# Revit family: NAU_Naughtone_Stng_HueWIP6
name_source: partatom
category: Furniture
revit_build: Autodesk Revit 2016 (Build: 20150714_1515(x64)
units: mm (PartAtom-declared; Revit-internal decimal feet)

## family parameters
Always vertical = Yes
Cut with Voids When Loaded = No
OmniClass Number = 23.40.20.00
OmniClass Title = General Furniture and Specialties
Room Calculation Point = No
Shared = Yes
Work Plane-Based = No

## types (4) — shared parameters
Assembly Code = E2020200
AssetType = Movable
Category = Pr_40_50_12 : Chairs, seats and benches
DurationUnit = year
ExpectedLife = 7
Finish = Fabric upholstery, wooden table top with oak/walnut veneer, white/black MFMDF top with reverse chamfer, white/black/RAL EPC steel frame
IfcExportAs = IfcFurnishingElementType
IfcExportType = CHAIR
Keynote = Pr_40_50_12
ManufacturerName = Naughtone
ManufacturerURL = www.naughtone.com/
Material = Fabric, plywood frame, foam, steel legs, wooden table top
NBSDescription = Seating
NBSReference = 45-35-72/352
NominalLength = 1870 mm
NominalWidth = 900 mm
ProductInformation = www.naughtone.com
Shape = Rectangular
SustainabilityPerformance = FSC certifeied, SCS indoor advantage gold
URL = www.naughtone.com
Uniclass2015Code = Pr_40_50_12
Uniclass2015Title = Chairs, seats and benches
Uniclass2015Version = Products v1.14
Version = 1
WarrantyDurationLabor = 7
WarrantyDurationParts = 7
WarrantyDurationUnit = year

## per-type parameters (varying)
| type | BIMObjectName | Description | HeightOfSeatingFrame | HighestSeatingHeight | IsHighLeg | IsLeg | IsPanel | LowestSeatingHeight | Model | ModelNumber | ModelReference | Name | NominalHeight | SeatingHeight | Size |
| Hue with steel legs HUEST 1870 x 900 x 750 mm | NAU_Naughtone_Seating_Hue_WithSteelLegs | Hue with steel legs - Hue is perfect for use in narrow spaces, and is ideally suited for pre and post meeting situations. | 284 mm | 450 mm  [stored 1.47638 ft] | No | Yes | No | 450 mm  [stored 1.47638 ft] | HUEST | HUEST | Hue with steel legs - Hue is perfect for use in narrow spaces, and is ideally suited for pre and post meeting situations. | Seating_Hue_WithSteelLegs_Naughtone | 750 mm  [stored 2.46063 ft] | 450 mm  [stored 1.47638 ft] | 1870 x 900 x 750 mm |
| Hue with screen and steel legs HUESST 1870 x 900 x 1495 mm | NAU_Naughtone_Seating_Hue_WithScreenandSteelLegs | Hue with screen and steel legs - Hue is perfect for use in narrow spaces, and is ideally suited for pre and post meeting situations. | 284 mm | 450 mm  [stored 1.47638 ft] | No | Yes | Yes | 450 mm  [stored 1.47638 ft] | HUESST | HUESST | Hue with screen and steel legs - Hue is perfect for use in narrow spaces, and is ideally suited for pre and post meeting situations. | Seating_Hue_WithScreenandSteelLegs_Naughtone | 1495 mm | 450 mm  [stored 1.47638 ft] | 1870 x 900 x 1495 mm |
| Hue bar height with steel legs HUEBHST 1870 x 900 x 1050 mm | NAU_Naughtone_Seating_Hue_BarHeightWithSteelLegs | Hue bar height with steel legs - Hue is perfect for use in narrow spaces, and is ideally suited for pre and post meeting situations. | 600 mm | 750 mm  [stored 2.46063 ft] | Yes | No | No | 750 mm  [stored 2.46063 ft] | HUEBHST | HUEBHST | Hue bar height with steel legs - Hue is perfect for use in narrow spaces, and is ideally suited for pre and post meeting situations. | Seating_Hue_BarHeightWithSteelLegs_Naughtone | 1050 mm | 750 mm  [stored 2.46063 ft] | 1870 x 900 x 1050 mm |
| Hue bar height with screen and steel legs HUEBHSST 1870 x 900 x 1795 mm | NAU_Naughtone_Seating_Hue_BarHeightWithScreenandSteelLegs | Hue bar height with screen and steel legs - Hue is perfect for use in narrow spaces, and is ideally suited for pre and post meeting situations. | 600 mm | 750 mm  [stored 2.46063 ft] | Yes | No | Yes | 750 mm  [stored 2.46063 ft] | HUEBHSST | HUEBHSST | Hue bar height with screen and steel legs - Hue is perfect for use in narrow spaces, and is ideally suited for pre and post meeting situations. | Seating_Hue_BarHeightWithScreenandSteelLegs_Naughtone | 1795 mm | 750 mm  [stored 2.46063 ft] | 1870 x 900 x 1795 mm |

note: [stored X ft] marks values corroborated as IEEE doubles in the binary element streams (Revit-internal decimal feet)

## geometry (parser evidence)
native form markers: Sweep x6
no freeform markers — native parametric forms only
